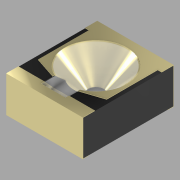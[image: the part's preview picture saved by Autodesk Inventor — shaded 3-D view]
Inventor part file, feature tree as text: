
AUTODESK INVENTOR PART (.ipt)
format: ipt  version: 2020 (Build 240168000, 168)  size: 292,352 bytes
history: native  units: mm
features: sketch x13, extrude x12, projected_geometry x7, mirror x2, plane x1, revolve x1, thicken_offset x1
ambient origin geometry x8: Origin, YZ Plane, XZ Plane, XY Plane, X Axis, Y Axis, Z Axis, Center Point
bodies: Solid1 (feature_tree), Solid2 (feature_tree), Solid3 (feature_tree)
feature tree (37):
  extrude  "Extrusion1"  Depth=2.3mm
  sketch  "Sketch2"  dims[d2=0.9mm d3=0.0mm d4=1.6mm]
  plane  "Work Plane1"
  revolve  "Revolution1"  [1 undecoded]
  extrude  "Extrusion2"  Depth=0.6mm
  extrude  "Extrusion6"  TaperAngle=90.0deg  [1 undecoded]
  extrude  "Extrusion3"  TaperAngle=0.0deg  [1 undecoded]
  extrude  "Extrusion4"  Depth=0.01mm
  extrude  "Extrusion7"  Depth=0.6mm
  extrude  "Extrusion5"  Depth=0.6mm
  mirror  "Mirror1"
  extrude  "Extrusion8"  Depth=1.65mm
  extrude  "Extrusion9"  Depth=0.3mm
  extrude  "Extrusion10"  Depth=1.3mm
  extrude  "Extrusion11"  Depth=0.1mm
  mirror  "Mirror2"
  extrude  "Extrusion12"  Depth=0.02mm
  thicken_offset  "Thicken1"
  sketch  "Sketch1"  dims[d0=1.95mm d1=2.3mm]
  sketch  "Sketch3"  dims[d5=1.0mm d6=0.6mm]
  sketch  "Sketch4"  dims[d7=0.2mm d8=90.0deg]
  projected_geometry  "Projected Loop1"
  sketch  "Sketch5"  dims[d9=0.6mm d10=0.0mm]
  projected_geometry  "Projected Loop2"
  sketch  "Sketch6"  dims[d11=0.01mm d12=0.15mm]
  sketch  "Sketch7"  dims[d13=0.15mm d14=0.6mm]
  projected_geometry  "Projected Loop3"
  sketch  "Sketch8"  dims[d15=0.0mm d16=0.6mm]
  sketch  "Sketch9"  dims[d17=0.0mm d18=1.65mm]
  projected_geometry  "Projected Loop4"
  projected_geometry  "Projected Loop5"
  projected_geometry  "Projected Loop6"
  sketch  "Sketch10"  dims[d19=0.25mm d20=0.0mm d21=0.3mm]
  projected_geometry  "Projected Loop7"
  sketch  "Sketch11"  dims[d22=0.3mm d23=1.3mm]
  sketch  "Sketch12"  dims[d24=0.1mm d25=0.1mm]
  sketch  "Sketch13"  dims[d26=0.65mm d27=1.0mm d28=0.2mm d29=0.05mm d30=0.24mm d31=0.0mm d32=0.3mm d33=0.0mm d34=0.05mm d35=0.05mm d36=0.24mm d37=0.0mm d38=0.01mm d39=0.0mm d40=0.01mm d41=0.0mm d42=0.01mm d43=0.0mm d44=0.01mm d45=0.0mm d46=0.02mm d47=0.02mm]
note: 3 required parameter values undecoded (feature->parameter linkage not recoverable at this tier; creation-order binding heuristic only, values carry confidence <= 0.55)